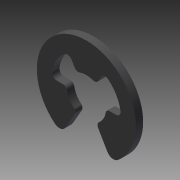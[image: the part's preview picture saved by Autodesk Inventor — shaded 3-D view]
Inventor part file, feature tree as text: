
AUTODESK INVENTOR PART (.ipt)
format: ipt  version: 2014 (Build 180170000, 170)  size: 131,584 bytes
history: native  units: in
note: dims shown in document units (in); Inventor stores cm internally (conversion verified against a paired STEP export)
features: other x7, extrude x1, sketch x1
ambient origin geometry x8: Origin, YZ Plane, XZ Plane, XY Plane, X Axis, Y Axis, Z Axis, Center Point
bodies: Solid1 (feature_tree)
feature tree (9):
  extrude  "Extrusion1"  [1 undecoded]
  other  "RR_XY"
  other  "RR_YZ"
  other  "RR_ZX"
  other  "RR_X"
  other  "RR_Y"
  other  "RR_Z"
  other  "RR_Center"
  sketch  "Sketch_1"  dims[d0=0.0275in d1=0.0in]
note: 1 required parameter value undecoded (feature->parameter linkage not recoverable at this tier; creation-order binding heuristic only, values carry confidence <= 0.55)
